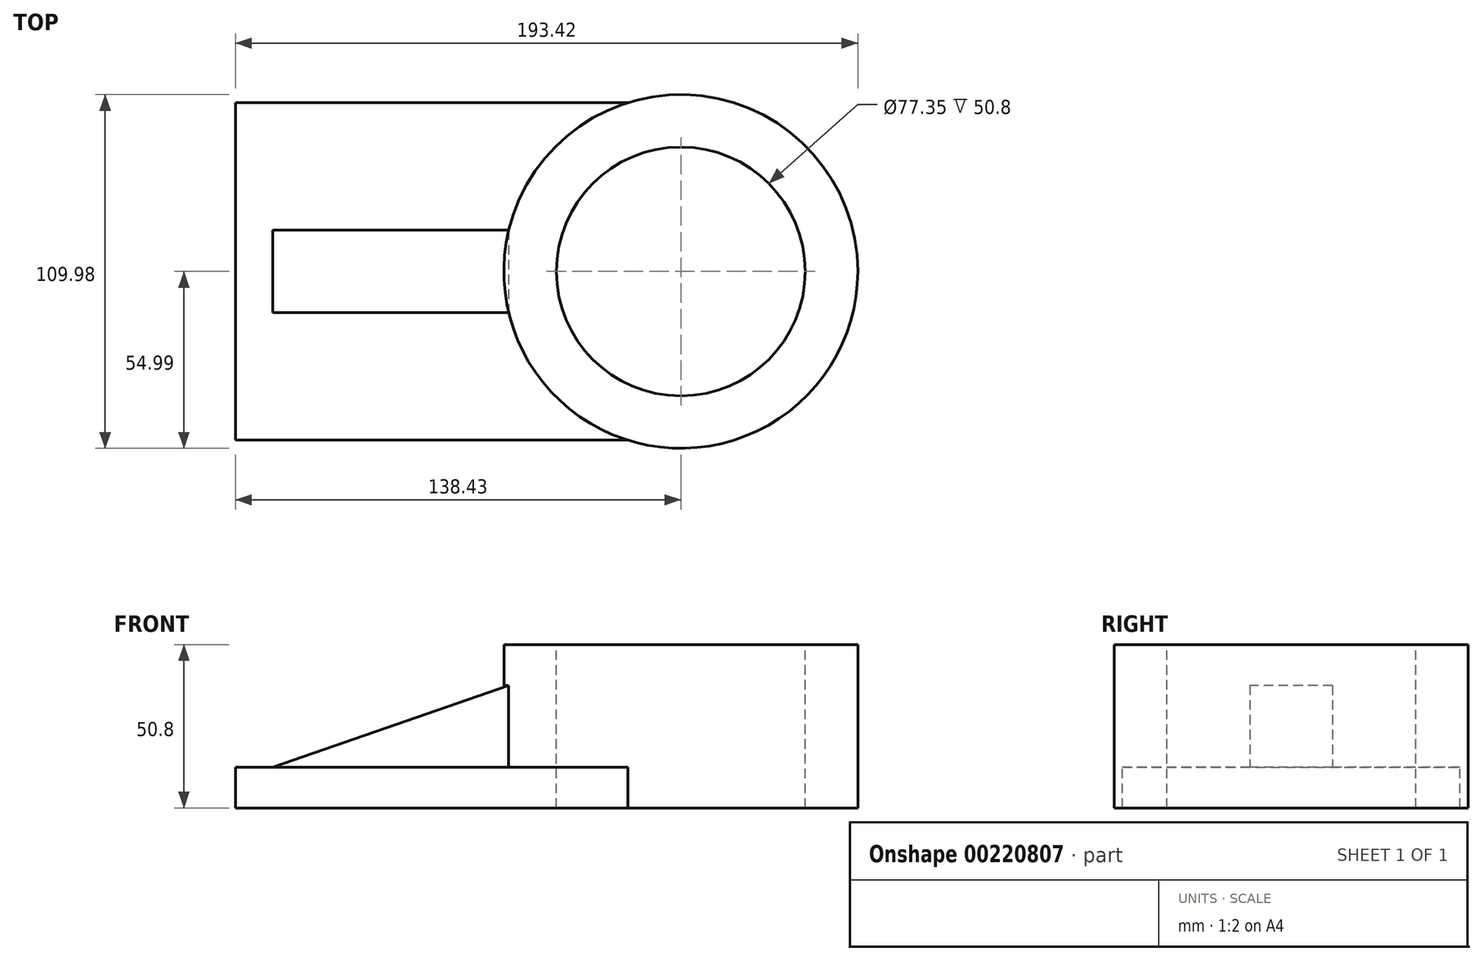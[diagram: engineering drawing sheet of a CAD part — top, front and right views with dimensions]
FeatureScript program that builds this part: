
annotation { "Feature Type Name" : "Feature", "Feature Type Description" : "" }
export const myFeature = defineFeature(function(context is Context, id is Id, definition is map)
    precondition{}
    {
        {
            var Q0;
            Q0=qCreatedBy(makeId("Top.planeOp"),FACE);
            var sketch = newSketch(context, id + "F0", { "sketchPlane" : qUnion([Q0])});
            skLineSegment(sketch, "E0.bottom", {"start": v(-76.55, -58.48) * mm, "end": v(45.43, -58.48) * mm});
            skLineSegment(sketch, "E0.top", {"start": v(-76.55, 58.12) * mm, "end": v(45.43, 58.12) * mm});
            skLineSegment(sketch, "E0.left", {"start": v(-76.55, -58.48) * mm, "end": v(-76.55, 58.12) * mm});
            skLineSegment(sketch, "E0.right", {"start": v(45.43, -58.48) * mm, "end": v(45.43, 58.12) * mm});
            skSolve(sketch);
        }
        {
            var Q0;
            Q0 = qSketchRegion(id + "F0", true);
            extrude(context, id + "F1", {"entities" : qUnion([Q0]), "depth" : 12.7 * mm});
        }
        {
            var Q0;
            Q0=qCreatedBy(makeId("Top.planeOp"),FACE);
            var sketch = newSketch(context, id + "F2", { "sketchPlane" : qUnion([Q0])});
            skCircle(sketch, "E1", {"center": v(61.88, 0) * mm, "radius": 54.99 * mm});
            skSolve(sketch);
        }
        {
            var Q0;
            Q0=makeQuery(id+"F2.imprint","IMPRINT",FACE,{"disambiguationData":[TD([[makeQuery(id+"F2.imprint","IMPRINT",EDGE,{"derivedFrom":sQuery(id+"F2.wireOp",EDGE,"E1")}),1.0]])]});
            extrude(context, id + "F3", {"entities" : qUnion([Q0]), "operationType" : NewBodyOperationType.ADD, "depth" : 50.8 * mm});
        }
        {
            var Q0;
            Q0=makeQuery(id+"F3.opExtrude","CAP_FACE",FACE,{"disambiguationData":[OSD([sQuery(id+"F2.wireOp",EDGE,"E1")])],"isStart":false});
            var sketch = newSketch(context, id + "F4", { "sketchPlane" : qUnion([Q0])});
            skCircle(sketch, "E2", {"center": v(61.88, 0) * mm, "radius": 38.68 * mm});
            skSolve(sketch);
        }
        {
            var Q0;
            Q0=makeQuery(id+"F4.imprint","IMPRINT",FACE,{"disambiguationData":[TD([[makeQuery(id+"F4.imprint","IMPRINT",EDGE,{"derivedFrom":sQuery(id+"F4.wireOp",EDGE,"E2")}),1.0]])]});
            extrude(context, id + "F5", {"entities" : qUnion([Q0]), "operationType" : NewBodyOperationType.REMOVE, "oppositeDirection" : true, "depth" : 101.6 * mm});
        }
        {
            var Q0;
            Q0=makeQuery(id+"F1.opExtrude","CAP_FACE",FACE,{"disambiguationData":[OSD([sQuery(id+"F0.wireOp",EDGE,"E0.bottom"),sQuery(id+"F0.wireOp",EDGE,"E0.top"),sQuery(id+"F0.wireOp",EDGE,"E0.left"),sQuery(id+"F0.wireOp",EDGE,"E0.right")])],"isStart":false});
            var sketch = newSketch(context, id + "F6", { "sketchPlane" : qUnion([Q0])});
            skLineSegment(sketch, "E3.bottom", {"start": v(8.4, 12.82) * mm, "end": v(-64.92, 12.82) * mm});
            skLineSegment(sketch, "E3.top", {"start": v(8.4, -12.82) * mm, "end": v(-64.92, -12.82) * mm});
            skLineSegment(sketch, "E3.left", {"start": v(8.4, 12.82) * mm, "end": v(8.4, -12.82) * mm});
            skLineSegment(sketch, "E3.right", {"start": v(-64.92, 12.82) * mm, "end": v(-64.92, -12.82) * mm});
            skPoint(sketch, "E3.middle", {"position": v(-28.26, 0) * mm});
            skSolve(sketch);
        }
        {
            var Q0;
            {var subQ0=sQuery(id+"F6.wireOp",EDGE,"E3.bottom");Q0=makeQuery(id+"F6.imprint","IMPRINT",FACE,{"disambiguationData":[TD([[makeQuery(id+"F6.imprint","IMPRINT",EDGE,{"derivedFrom":subQ0}),1.0]])]});}
            extrude(context, id + "F7", {"entities" : qUnion([Q0]), "operationType" : NewBodyOperationType.ADD, "depth" : 25.4 * mm});
        }
        {
            var Q0;
            Q0=makeQuery(id+"F7.opExtrude","SWEPT_FACE",FACE,{"disambiguationData":[OSD([sQuery(id+"F6.wireOp",EDGE,"E3.top")])]});
            var sketch = newSketch(context, id + "F8", { "sketchPlane" : qUnion([Q0])});
            skLineSegment(sketch, "E4", {"start": v(8.4, 38.1) * mm, "end": v(-64.92, 12.7) * mm});
            skLineSegment(sketch, "E5", {"start": v(-64.92, 38.1) * mm, "end": v(8.4, 38.1) * mm});
            skLineSegment(sketch, "E6", {"start": v(-64.92, 38.1) * mm, "end": v(-64.92, 12.7) * mm});
            skSolve(sketch);
        }
        {
            var Q0;
            Q0=makeQuery(id+"F8.imprint","IMPRINT",FACE,{"disambiguationData":[TD([[makeQuery(id+"F8.imprint","IMPRINT",EDGE,{"derivedFrom":sQuery(id+"F8.wireOp",EDGE,"E4")}),-1.0]])]});
            extrude(context, id + "F9", {"entities" : qUnion([Q0]), "operationType" : NewBodyOperationType.REMOVE, "oppositeDirection" : true, "depth" : 50.8 * mm});
        }
        {
            var Q0;
            Q0=makeQuery(id+"F1.opExtrude","CAP_FACE",FACE,{"disambiguationData":[OSD([sQuery(id+"F0.wireOp",EDGE,"E0.bottom"),sQuery(id+"F0.wireOp",EDGE,"E0.top"),sQuery(id+"F0.wireOp",EDGE,"E0.left"),sQuery(id+"F0.wireOp",EDGE,"E0.right")])],"isStart":false});
            var sketch = newSketch(context, id + "F10", { "sketchPlane" : qUnion([Q0])});
            skLineSegment(sketch, "E7.bottom", {"start": v(-76.55, -58.48) * mm, "end": v(45.43, -58.48) * mm});
            skLineSegment(sketch, "E7.top", {"start": v(-76.55, -52.47) * mm, "end": v(45.43, -52.47) * mm});
            skLineSegment(sketch, "E7.left", {"start": v(-76.55, -58.48) * mm, "end": v(-76.55, -52.47) * mm});
            skLineSegment(sketch, "E7.right", {"start": v(45.43, -58.48) * mm, "end": v(45.43, -52.47) * mm});
            skSolve(sketch);
        }
        {
            var Q0;
            Q0=makeQuery(id+"F10.imprint","IMPRINT",FACE,{"disambiguationData":[TD([[makeQuery(id+"F10.imprint","IMPRINT",EDGE,{"derivedFrom":sQuery(id+"F10.wireOp",EDGE,"E7.bottom")}),1.0]])]});
            extrude(context, id + "F11", {"entities" : qUnion([Q0]), "operationType" : NewBodyOperationType.REMOVE, "oppositeDirection" : true, "depth" : 25.4 * mm});
        }
        {
            var Q0;
            Q0=makeQuery(id+"F1.opExtrude","CAP_FACE",FACE,{"disambiguationData":[OSD([sQuery(id+"F0.wireOp",EDGE,"E0.bottom"),sQuery(id+"F0.wireOp",EDGE,"E0.top"),sQuery(id+"F0.wireOp",EDGE,"E0.left"),sQuery(id+"F0.wireOp",EDGE,"E0.right")])],"isStart":false});
            var sketch = newSketch(context, id + "F12", { "sketchPlane" : qUnion([Q0])});
            skLineSegment(sketch, "E8.bottom", {"start": v(-76.55, 58.12) * mm, "end": v(45.43, 58.12) * mm});
            skLineSegment(sketch, "E8.top", {"start": v(-76.55, 52.47) * mm, "end": v(45.43, 52.47) * mm});
            skLineSegment(sketch, "E8.left", {"start": v(-76.55, 58.12) * mm, "end": v(-76.55, 52.47) * mm});
            skLineSegment(sketch, "E8.right", {"start": v(45.43, 58.12) * mm, "end": v(45.43, 52.47) * mm});
            skSolve(sketch);
        }
        {
            var Q0;
            Q0=makeQuery(id+"F12.imprint","IMPRINT",FACE,{"disambiguationData":[TD([[makeQuery(id+"F12.imprint","IMPRINT",EDGE,{"derivedFrom":sQuery(id+"F12.wireOp",EDGE,"E8.bottom")}),-1.0]])]});
            extrude(context, id + "F13", {"entities" : qUnion([Q0]), "operationType" : NewBodyOperationType.REMOVE, "oppositeDirection" : true, "depth" : 25.4 * mm});
        }
    });
